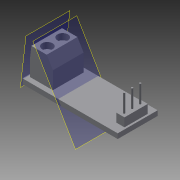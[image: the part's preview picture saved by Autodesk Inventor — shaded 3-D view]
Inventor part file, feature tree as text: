
AUTODESK INVENTOR PART (.ipt)
format: ipt  version: 2015 (Build 190159000, 159)  size: 178,176 bytes
history: native  units: in
note: dims shown in document units (in); Inventor stores cm internally (conversion verified against a paired STEP export)
features: extrude x9, sketch x9, plane x2, fillet x1
ambient origin geometry x8: Origin, YZ Plane, XZ Plane, XY Plane, X Axis, Y Axis, Z Axis, Center Point
bodies: Solid1 (feature_tree)
feature tree (21):
  extrude  "Extrusion1"  Depth=0.5118in
  extrude  "Extrusion2"  Depth=0.1102in TaperAngle=0.0deg
  extrude  "Extrusion3"  Depth=0.2992in
  extrude  "Extrusion4"  Depth=0.0236in
  extrude  "Extrusion5"  Depth=0.0236in
  plane  "Work Plane1"
  extrude  "Extrusion6"  Depth=0.0236in
  plane  "Work Plane2"
  extrude  "Extrusion7"  Depth=0.0512in
  extrude  "Extrusion8"  Depth=0.0787in
  extrude  "Extrusion9"  Depth=0.2283in TaperAngle=0.0deg
  fillet  "Fillet1"  Radius=0.2913in
  sketch  "Sketch1"  dims[d0=1.2205in d1=0.5118in]
  sketch  "Sketch2"  dims[d2=0.063in d3=0.0in d7=0.1102in d8=0.0in]
  sketch  "Sketch3"  dims[d9=0.1024in d10=0.2992in]
  sketch  "Sketch4"  dims[d12=0.1024in d13=0.0236in]
  sketch  "Sketch5"  dims[d14=0.0236in d15=0.0236in]
  sketch  "Sketch6"  dims[d16=0.0236in d17=0.0512in]
  sketch  "Sketch7"  dims[d18=0.0512in d19=0.0512in]
  sketch  "Sketch8"  dims[d20=0.0787in d21=0.0787in]
  sketch  "Sketch9"  dims[d22=0.0472in d23=0.2283in d24=0.0in d25=0.2913in d26=0.3937in d27=0.0354in d28=0.063in d29=0.2205in d30=0.0in d31=0.1969in d32=0.0in d33=0.0in d34=0.0787in d35=0.1339in d36=0.0in d37=0.0394in d38=0.0in d39=0.0787in d40=0.0in d41=0.1339in d42=0.1339in d43=0.0984in d44=0.1969in d45=0.1063in d46=0.1063in d47=0.0787in d48=0.0in d49=0.1575in d50=0.1969in d51=0.0787in d52=0.1575in d53=0.0551in d54=0.0in d55=0.0079in]
